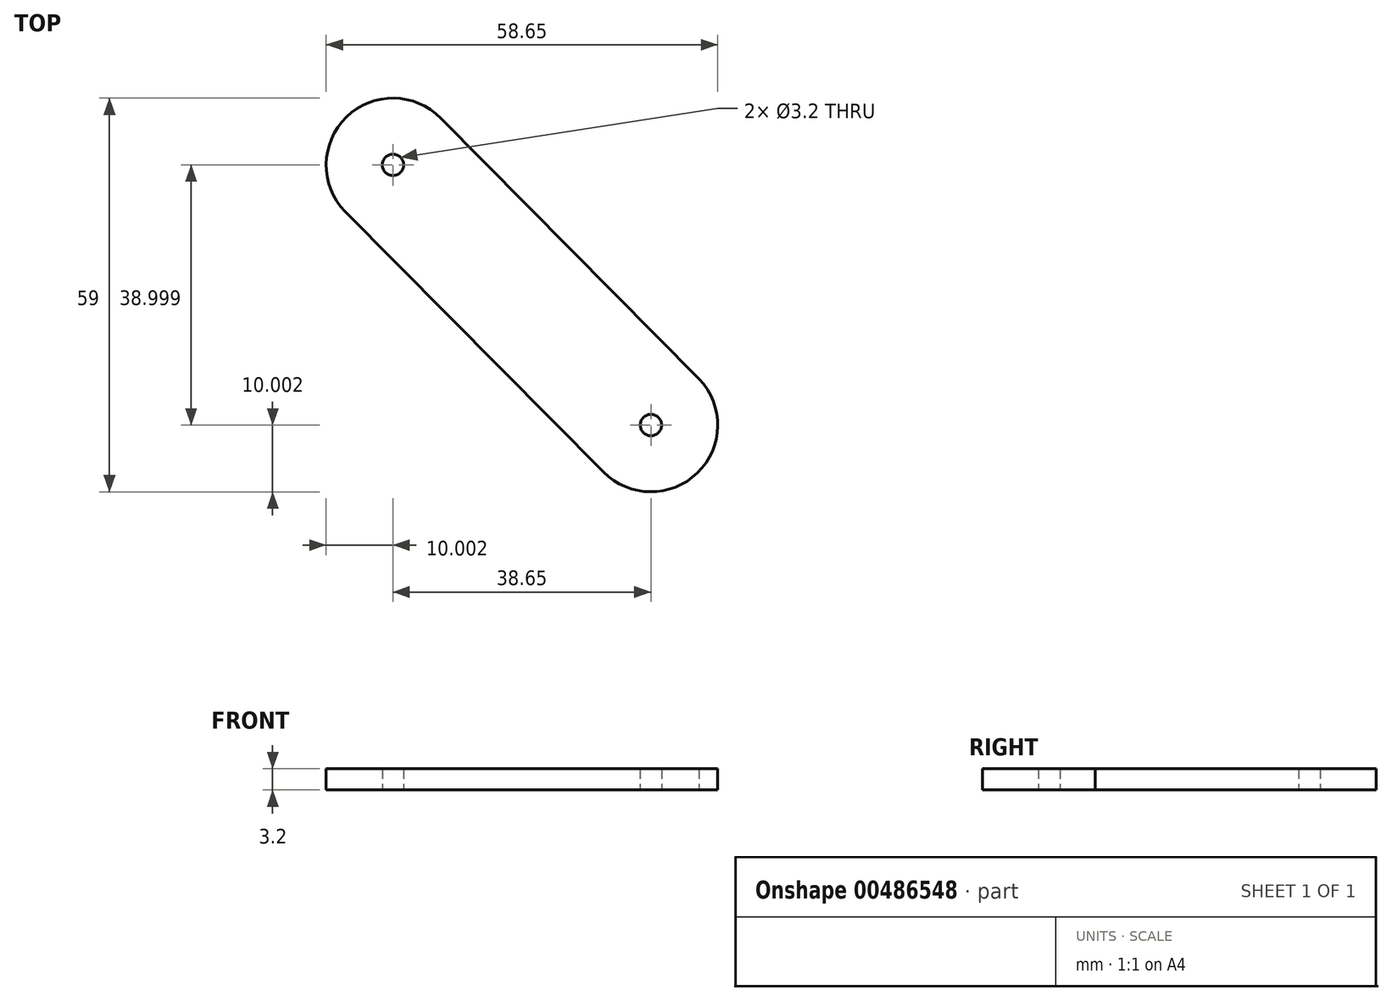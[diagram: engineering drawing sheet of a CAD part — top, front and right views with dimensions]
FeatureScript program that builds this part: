
annotation { "Feature Type Name" : "Feature", "Feature Type Description" : "" }
export const myFeature = defineFeature(function(context is Context, id is Id, definition is map)
    precondition{}
    {
        {
            var Q0;
            Q0=qCreatedBy(makeId("Top.planeOp"),FACE);
            var sketch = newSketch(context, id + "F0", { "sketchPlane" : qUnion([Q0])});
            skLineSegment(sketch, "E0", {"start": v(-18.14, -25.1) * mm, "end": v(-56.86, 13.97) * mm});
            skLineSegment(sketch, "E1", {"start": v(-42.52, 27.91) * mm, "end": v(-3.8, -11.15) * mm});
            skArc(sketch, "E2", {"start": v(-18.14, -25.1) * mm, "mid": v(-4.07, -25.23) * mm, "end": v(-3.8, -11.15) * mm});
            skArc(sketch, "E3", {"start": v(-42.52, 27.91) * mm, "mid": v(-56.66, 28.11) * mm, "end": v(-56.86, 13.97) * mm});
            skCircle(sketch, "E4", {"center": v(-11.04, -18.06) * mm, "radius": 1.6 * mm});
            skCircle(sketch, "E5", {"center": v(-49.69, 20.94) * mm, "radius": 1.6 * mm});
            skSolve(sketch);
        }
        {
            var Q0;
            Q0=makeQuery(id+"F0.imprint","IMPRINT",FACE,{"disambiguationData":[TD([[makeQuery(id+"F0.imprint","IMPRINT",EDGE,{"derivedFrom":sQuery(id+"F0.wireOp",EDGE,"E0")}),-1.0]])]});
            extrude(context, id + "F1", {"entities" : qUnion([Q0]), "depth" : 3.2 * mm, "offsetDistance" : 25 * mm});
        }
    });
